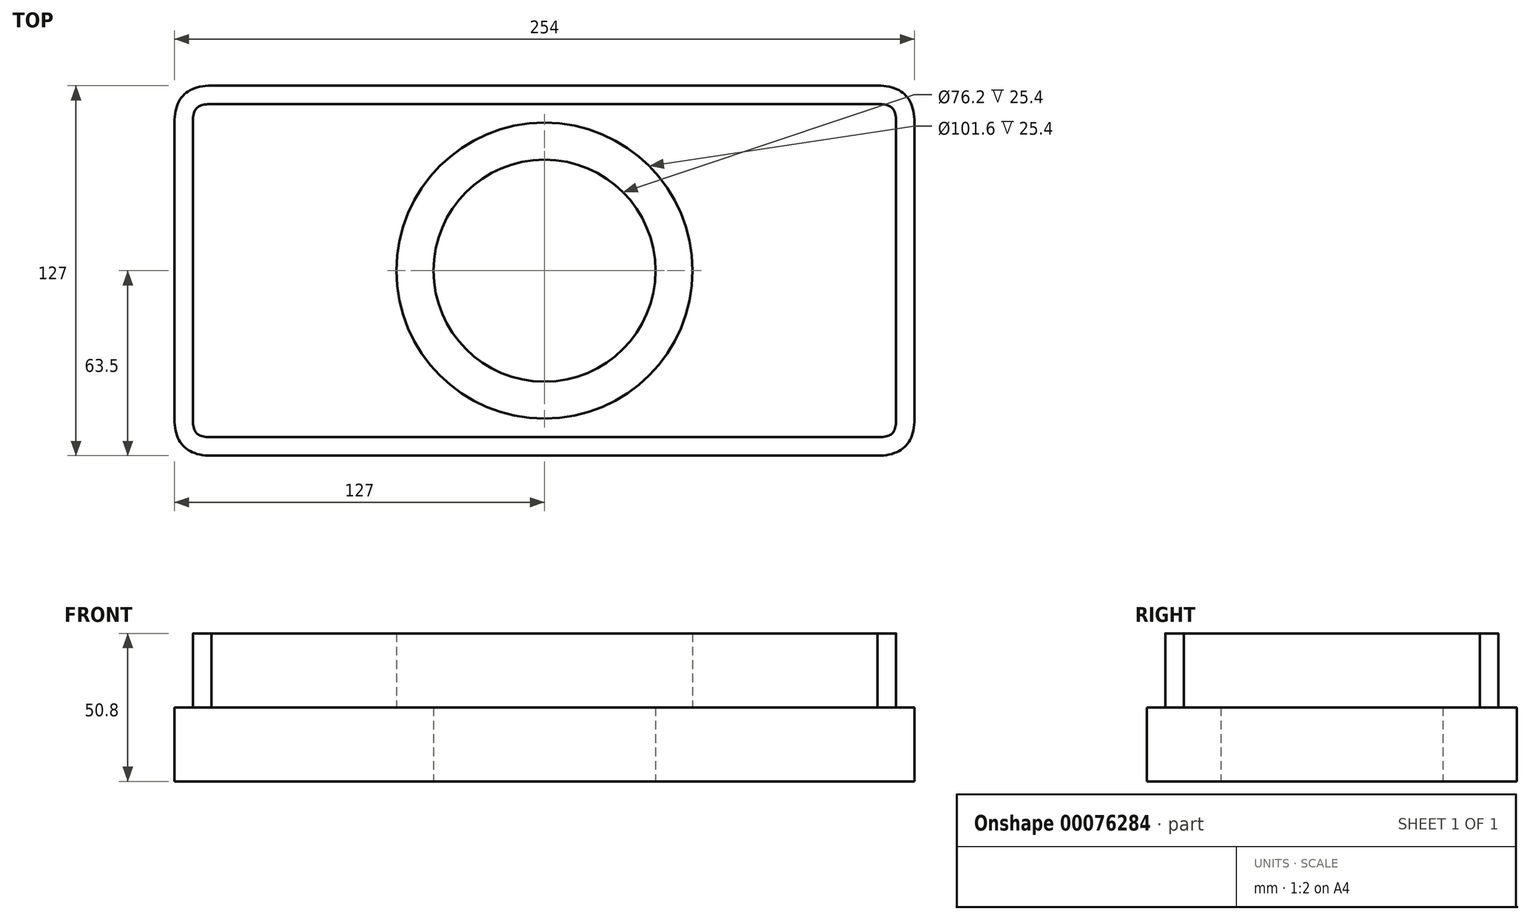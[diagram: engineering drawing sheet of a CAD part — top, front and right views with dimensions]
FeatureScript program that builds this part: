
annotation { "Feature Type Name" : "Feature", "Feature Type Description" : "" }
export const myFeature = defineFeature(function(context is Context, id is Id, definition is map)
    precondition{}
    {
        {
            var Q0;
            Q0=qCreatedBy(makeId("Top.planeOp"),FACE);
            var sketch = newSketch(context, id + "F0", { "sketchPlane" : qUnion([Q0])});
            skLineSegment(sketch, "E0.bottom", {"start": v(-127, -63.5) * mm, "end": v(127, -63.5) * mm});
            skLineSegment(sketch, "E0.top", {"start": v(-127, 63.5) * mm, "end": v(127, 63.5) * mm});
            skLineSegment(sketch, "E0.left", {"start": v(-127, -63.5) * mm, "end": v(-127, 63.5) * mm});
            skLineSegment(sketch, "E0.right", {"start": v(127, -63.5) * mm, "end": v(127, 63.5) * mm});
            skLineSegment(sketch, "E1", {"start": v(-127, 63.5) * mm, "end": v(127, -63.5) * mm, "construction": true});
            skCircle(sketch, "E2", {"center": v(0, 0) * mm, "radius": 38.1 * mm});
            skSolve(sketch);
        }
        {
            var Q0;
            Q0=makeQuery(id+"F0.imprint","IMPRINT",FACE,{"disambiguationData":[TD([[makeQuery(id+"F0.imprint","IMPRINT",EDGE,{"derivedFrom":sQuery(id+"F0.wireOp",EDGE,"E0.bottom")}),1.0]])]});
            extrude(context, id + "F1", {"entities" : qUnion([Q0]), "depth" : 25.4 * mm});
        }
        {
            var Q0;
            Q0=makeQuery(id+"F1.opExtrude","SWEPT_EDGE",EDGE,{"disambiguationData":[OSD([sQuery(id+"F0.wireOp",EDGE,"E0.bottom"),sQuery(id+"F0.wireOp",EDGE,"E0.right")])]});
            var Q1;
            Q1=makeQuery(id+"F1.opExtrude","SWEPT_EDGE",EDGE,{"disambiguationData":[OSD([sQuery(id+"F0.wireOp",EDGE,"E0.top"),sQuery(id+"F0.wireOp",EDGE,"E0.right")])]});
            var Q2;
            Q2=makeQuery(id+"F1.opExtrude","SWEPT_EDGE",EDGE,{"disambiguationData":[OSD([sQuery(id+"F0.wireOp",EDGE,"E0.bottom"),sQuery(id+"F0.wireOp",EDGE,"E0.left")])]});
            var Q3;
            Q3=makeQuery(id+"F1.opExtrude","SWEPT_EDGE",EDGE,{"disambiguationData":[OSD([sQuery(id+"F0.wireOp",EDGE,"E0.top"),sQuery(id+"F0.wireOp",EDGE,"E0.left")])]});
            fillet(context, id + "F2", {"entities" : qUnion([Q0, Q1, Q2, Q3]), "radius" : 12.7 * mm, "tangentPropagation" : true, "rho" : 0.5, "crossSection" : FilletCrossSection.CONIC, "allowEdgeOverflow" : false});
        }
        {
            var Q0;
            Q0=makeQuery(id+"F1.opExtrude","CAP_FACE",FACE,{"disambiguationData":[OSD([sQuery(id+"F0.wireOp",EDGE,"E0.bottom"),sQuery(id+"F0.wireOp",EDGE,"E0.top"),sQuery(id+"F0.wireOp",EDGE,"E0.left"),sQuery(id+"F0.wireOp",EDGE,"E0.right"),sQuery(id+"F0.wireOp",EDGE,"E2")])],"isStart":false});
            var sketch = newSketch(context, id + "F3", { "sketchPlane" : qUnion([Q0])});
            skFitSpline(sketch, "E3.0", {"points": [v(-114.3, 57.15) * mm, v(-115.1, 57.15) * mm, v(-116.48, 57.05) * mm, v(-117.94, 56.7) * mm, v(-118.83, 56.27) * mm, v(-119.35, 55.85) * mm, v(-119.77, 55.33) * mm, v(-120.2, 54.44) * mm, v(-120.55, 52.98) * mm, v(-120.65, 51.6) * mm, v(-120.65, 50.8) * mm]});
            skLineSegment(sketch, "E3.1", {"start": v(114.3, 57.15) * mm, "end": v(-114.3, 57.15) * mm});
            skLineSegment(sketch, "E3.2", {"start": v(-120.65, 50.8) * mm, "end": v(-120.65, -50.8) * mm});
            skFitSpline(sketch, "E3.3", {"points": [v(120.65, 50.8) * mm, v(120.65, 51.6) * mm, v(120.55, 52.98) * mm, v(120.2, 54.44) * mm, v(119.77, 55.33) * mm, v(119.35, 55.85) * mm, v(118.83, 56.27) * mm, v(117.94, 56.7) * mm, v(116.48, 57.05) * mm, v(115.1, 57.15) * mm, v(114.3, 57.15) * mm]});
            skFitSpline(sketch, "E3.4", {"points": [v(-120.65, -50.8) * mm, v(-120.65, -51.6) * mm, v(-120.55, -52.98) * mm, v(-120.2, -54.44) * mm, v(-119.77, -55.33) * mm, v(-119.35, -55.85) * mm, v(-118.83, -56.27) * mm, v(-117.94, -56.7) * mm, v(-116.48, -57.05) * mm, v(-115.1, -57.15) * mm, v(-114.3, -57.15) * mm]});
            skLineSegment(sketch, "E3.5", {"start": v(-114.3, -57.15) * mm, "end": v(114.3, -57.15) * mm});
            skFitSpline(sketch, "E3.6", {"points": [v(114.3, -57.15) * mm, v(115.1, -57.15) * mm, v(116.48, -57.05) * mm, v(117.94, -56.7) * mm, v(118.83, -56.27) * mm, v(119.35, -55.85) * mm, v(119.77, -55.33) * mm, v(120.2, -54.44) * mm, v(120.55, -52.98) * mm, v(120.65, -51.6) * mm, v(120.65, -50.8) * mm]});
            skLineSegment(sketch, "E3.7", {"start": v(120.65, -50.8) * mm, "end": v(120.65, 50.8) * mm});
            skCircle(sketch, "E4.0", {"center": v(0, 0) * mm, "radius": 50.8 * mm});
            skSolve(sketch);
        }
        {
            var Q0;
            Q0 = qSketchRegion(id + "F3", true);
            extrude(context, id + "F4", {"entities" : qUnion([Q0]), "operationType" : NewBodyOperationType.ADD, "depth" : 25.4 * mm});
        }
    });
